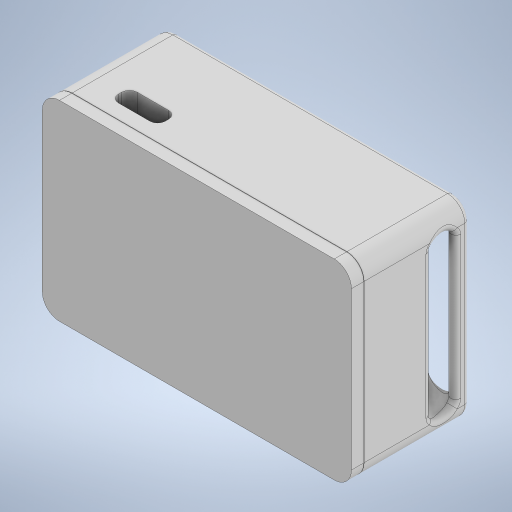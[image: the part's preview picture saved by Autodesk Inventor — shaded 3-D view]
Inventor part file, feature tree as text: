
AUTODESK INVENTOR PART (.ipt)
format: ipt  version: 2024.3 (Build 283343000, 343)  size: 763,904 bytes
history: native  units: in
note: dims shown in document units (in); Inventor stores cm internally (conversion verified against a paired STEP export)
features: reference x28, extrude x10, sketch x10, projected_geometry x10, fillet x9, other x9, plane x4, chamfer x3, shell x1
ambient origin geometry x8: Origin, YZ Plane, XZ Plane, XY Plane, X Axis, Y Axis, Z Axis, Center Point
bodies: Solid1 (feature_tree), Solid2 (feature_tree)
feature tree (84):
  extrude  "Extrusion1"  Depth=0.0787in TaperAngle=0.0deg
  fillet  "Fillet4"  [1 undecoded]
  extrude  "Extrusion2"  Depth=0.0394in
  fillet  "Fillet1"  Radius=1.2598in
  fillet  "Fillet2"  Radius=1.5354in
  fillet  "Fillet3"  Radius=2.4803in
  shell  "Shell1"  Thickness=0.0591in
  extrude  "Extrusion3"  Depth=0.0787in
  extrude  "Extrusion4"  Depth=0.1378in
  chamfer  "Chamfer1"  [1 undecoded]
  fillet  "Fillet5"  Radius=0.0591in
  extrude  "Extrusion5"  Depth=0.0197in
  plane  "Work Plane2"
  sketch  "Sketch6"  dims[d18=0.0118in]
  plane  "Work Plane1"
  extrude  "Extrusion7"  Depth=0.0394in TaperAngle=45.0deg
  chamfer  "Chamfer2"  Distance=0.0236in
  extrude  "Extrusion8"  Depth=0.0394in
  fillet  "Fillet9"  Radius=0.0118in
  fillet  "Fillet10"  Radius=0.0787in
  fillet  "Fillet11"  Radius=0.0118in
  plane  "Work Plane3"
  plane  "Work Plane4"
  extrude  "Extrusion11"  Depth=0.0394in
  fillet  "Fillet12"  Radius=0.5512in
  extrude  "Extrusion9"  Depth=0.0394in
  extrude  "Extrusion10"  Depth=0.0787in
  other  "Lip1"
  other  "Lip2"
  sketch  "Sketch1"  dims[d0=0.0787in d1=0.7874in d2=0.0in d3=45.0deg]
  sketch  "Sketch2"  dims[d4=0.1181in d5=0.1181in d6=1.2598in d7=0.0in d8=1.5354in d9=2.4803in d11=0.0591in d12=0.0394in]
  reference  "Reference1"
  reference  "Reference2"
  sketch  "Sketch3"  dims[d13=0.0394in d14=0.0787in]
  reference  "Reference3"
  sketch  "Sketch4"  dims[d15=0.1378in d16=0.0118in]
  projected_geometry  "Projected Loop1"
  sketch  "Sketch5"  dims[d17=0.0118in]
  reference  "Reference4"
  reference  "Reference5"
  reference  "Reference6"
  reference  "Reference7"
  reference  "Reference8"
  reference  "Reference9"
  reference  "Reference10"
  projected_geometry  "Projected Loop2"
  projected_geometry  "Projected Loop3"
  sketch  "Sketch7"  dims[d19=0.0118in]
  projected_geometry  "Projected Loop4"
  reference  "Reference11"
  projected_geometry  "Projected Loop5"
  sketch  "Sketch8"  dims[d20=0.0118in d21=0.0in d22=0.0in d23=0.0591in]
  projected_geometry  "Projected Loop6"
  sketch  "Sketch9"  dims[d24=0.0197in d25=0.0197in]
  projected_geometry  "Projected Loop7"
  sketch  "Sketch10"  dims[d26=0.0787in d27=0.0in d28=0.0394in d29=0.0787in d30=45.0deg d31=0.0236in d32=0.0118in d33=0.0118in d34=0.0787in d35=0.0118in d36=0.0118in d37=0.5512in d38=0.0in d41=0.2718in d46=0.0787in d47=0.2756in d48=0.0in d49=-0.4293in d50=0.2718in d51=0.0098in d52=45.0deg d55=0.7874in d56=0.3937in d57=0.0in d58=0.1969in d59=0.0787in d60=0.1575in d61=0.1575in d62=0.0in d63=0.0984in d64=-0.2061in d65=0.0591in d66=0.0354in d67=0.0in d68=0.0in d69=15.0deg d70=0.0in d71=0.0591in d72=0.0394in d73=0.0in d74=0.0in d75=15.0deg d76=0.0in d77=0.0039in d78=0.0787in d79=0.3937in d80=0.0in d81=0.0394in d40=0.0in d42=0.0in]
  projected_geometry  "Projected Loop8"
  projected_geometry  "Projected Loop9"
  reference  "Reference12"
  reference  "Reference13"
  reference  "Reference14"
  reference  "Reference15"
  reference  "Reference16"
  reference  "Reference17"
  reference  "Reference18"
  reference  "Reference19"
  reference  "Reference20"
  reference  "Reference21"
  reference  "Reference22"
  reference  "Reference23"
  reference  "Reference24"
  reference  "Reference25"
  reference  "Reference26"
  reference  "Reference27"
  reference  "Reference28"
  projected_geometry  "Project Cut Edges1"
  other  "Assembly9"
  other  "PCB:1"
  other  "PCB-V1:1"
  other  "LP112527-3.7V650mAh:1"
  other  "XIAO-nRF52840 v15:1"
  other  "USB TYPE C PORT:1"
  other  "USB TYPE C PORT (1):1"
  chamfer  "CHAMFER9:1"  Distance=0.2756in
note: 2 required parameter values undecoded (feature->parameter linkage not recoverable at this tier; creation-order binding heuristic only, values carry confidence <= 0.55)
